# Revit family: 11
name_source: partatom
category: Lighting Fixtures
revit_build: Autodesk Revit 2014 (Build: 20130308_1515(x64)
units: mm (PartAtom-declared; Revit-internal decimal feet)

## types (1)
- P500214-031
    Apparent Load = 60 VA
    Assembly Code = D5020200
    Default Elevation = 48 "
    Description = Offer a modern spin on a timeless design with the Parkhurst Collection. Lantern-style metal frames create an airy structure ideal for emitting ambient light over memories being made below. Inside the frame perch smooth, simple light bases ready to offer your home a lovely glow.
    Features = An open-cage metal frame creates a sophisticated, airy structure.
A beautiful black finish coats the lantern-style frame for an eye-pleasing, handsome design.
Inside the frame perch smooth, simple light bases ready to offer your home a lovely glow.
Ideal for a hallway, foyer, entryway, kitchen, or dining room.
Perfect for transitional, new traditional, and farmhouse settings.
Measures 14-3/8-inch width by 24-3/8-inch height.
Uses four candelabra base bulbs that are sold separately (60w max - LED or incandescent).
Able to be fully dimmable with dimmable bulbs.
Includes installation instructions and mounting hardware.
Progress Lighting products are designed for exceptional quality, reliability, and functionality.
    Fixture distribution = Direct
    Glass = Paint - Hubbell - White Texture
    Gold = Hubbell - Gold
    Height = 26.5 "
    Housing Material = Paint - Hubbell - Textured Camera Black
    Lamp = LED or Medium Base
    Load Classification = Lighting
    Manufacturer = Progress Lighting
    Model = P500214-031
    Power Factor = 1
    Product Documentation Link = https://hubbellcdn.com
    Product Link = https://www.hubbell.com
    URL = https://www.hubbell.com
    Voltage = 120 V
    Warranty = 1 year Warranty
    Wattage Comments = 60W
    Watts = 60 W
    Width = 6 "

## geometry (parser evidence)
native form markers: Sweep x6
no freeform markers — native parametric forms only
